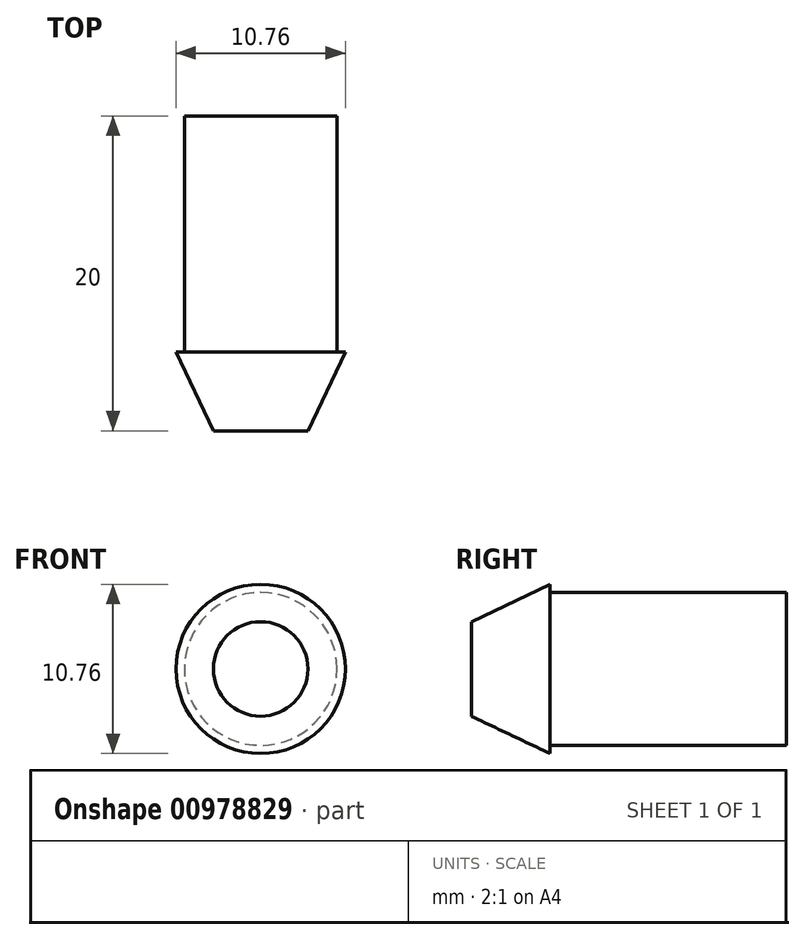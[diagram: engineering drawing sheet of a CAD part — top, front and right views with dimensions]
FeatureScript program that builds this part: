
annotation { "Feature Type Name" : "Feature", "Feature Type Description" : "" }
export const myFeature = defineFeature(function(context is Context, id is Id, definition is map)
    precondition{}
    {
        {
            var Q0;
            Q0=qCreatedBy(makeId("Front.planeOp"),FACE);
            var sketch = newSketch(context, id + "F0", { "sketchPlane" : qUnion([Q0])});
            skCircle(sketch, "E0", {"center": v(0, 0) * mm, "radius": 4.85 * mm});
            skSolve(sketch);
        }
        {
            var Q0;
            Q0 = qSketchRegion(id + "F0", true);
            extrude(context, id + "F1", {"entities" : qUnion([Q0]), "depth" : 15 * mm, "offsetDistance" : 25 * mm});
        }
        {
            var Q0;
            Q0=qCreatedBy(makeId("Front.planeOp"),FACE);
            cPlane(context, id + "F2", {"entities" : qUnion([Q0]), "cplaneType" : CPlaneType.OFFSET, "offset" : 15 * mm, "width" : 150 * mm, "height" : 150 * mm});
        }
        {
            var Q0;
            Q0=qCreatedBy(id+"F2.planeOp",FACE);
            var sketch = newSketch(context, id + "F3", { "sketchPlane" : qUnion([Q0])});
            skCircle(sketch, "E1", {"center": v(0, 0) * mm, "radius": 5.38 * mm});
            skSolve(sketch);
        }
        {
            var Q0;
            Q0=qCreatedBy(makeId("Front.planeOp"),FACE);
            cPlane(context, id + "F4", {"entities" : qUnion([Q0]), "cplaneType" : CPlaneType.OFFSET, "offset" : 20 * mm, "width" : 150 * mm, "height" : 150 * mm});
        }
        {
            var Q0;
            Q0=qCreatedBy(id+"F4.planeOp",FACE);
            var sketch = newSketch(context, id + "F5", { "sketchPlane" : qUnion([Q0])});
            skCircle(sketch, "E2", {"center": v(0, 0) * mm, "radius": 3 * mm});
            skSolve(sketch);
        }
        {
            var Q1;
            Q1=makeQuery(id+"F5.imprint","IMPRINT",FACE,{"disambiguationData":[TD([[makeQuery(id+"F5.imprint","IMPRINT",EDGE,{"derivedFrom":sQuery(id+"F5.wireOp",EDGE,"E2")}),1.0]])]});
            var Q2;
            Q2=makeQuery(id+"F3.imprint","IMPRINT",FACE,{"disambiguationData":[TD([[makeQuery(id+"F3.imprint","IMPRINT",EDGE,{"derivedFrom":sQuery(id+"F3.wireOp",EDGE,"E1")}),1.0]])]});
            loft(context, id + "F6", {"operationType" : NewBodyOperationType.ADD, "sheetProfilesArray" : [{ "sheetProfileEntities" : qUnion([Q1]) }, { "sheetProfileEntities" : qUnion([Q2]) }]});
        }
    });
